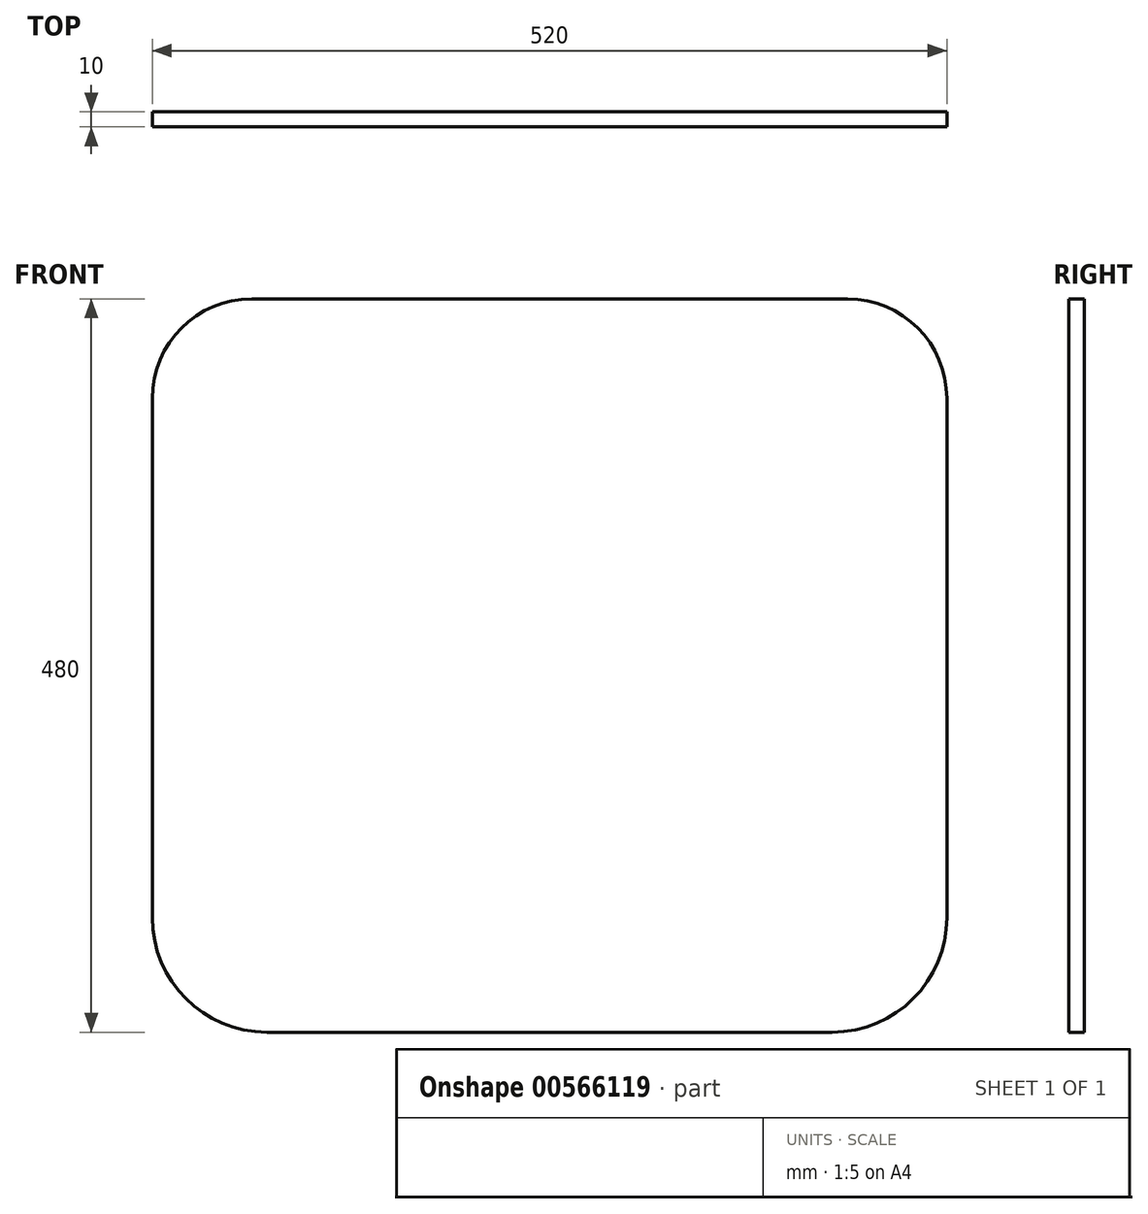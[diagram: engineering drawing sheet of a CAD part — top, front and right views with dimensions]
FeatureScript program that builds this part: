
annotation { "Feature Type Name" : "Feature", "Feature Type Description" : "" }
export const myFeature = defineFeature(function(context is Context, id is Id, definition is map)
    precondition{}
    {
        {
            var Q0;
            Q0=qCreatedBy(makeId("Front.planeOp"),FACE);
            var sketch = newSketch(context, id + "F0", { "sketchPlane" : qUnion([Q0])});
            skPoint(sketch, "E0.middle", {"position": v(0, 0) * mm});
            skPoint(sketch, "E1.visualSharp", {"position": v(-250, 300) * mm});
            skPoint(sketch, "E2.visualSharp", {"position": v(250, 300) * mm});
            skPoint(sketch, "E3.visualSharp", {"position": v(-250, -300) * mm});
            skPoint(sketch, "E4.visualSharp", {"position": v(250, -300) * mm});
            skLineSegment(sketch, "E5.0", {"start": v(260, 105) * mm, "end": v(260, -235) * mm});
            skLineSegment(sketch, "E5.3", {"start": v(-185, -310) * mm, "end": v(185, -310) * mm});
            skArc(sketch, "E5.4", {"start": v(-260, -235) * mm, "mid": v(-238.03, -288.03) * mm, "end": v(-185, -310) * mm});
            skLineSegment(sketch, "E5.5", {"start": v(-260, 105) * mm, "end": v(-260, -235) * mm});
            skArc(sketch, "E6.0", {"start": v(185, -310) * mm, "mid": v(238.03, -288.03) * mm, "end": v(260, -235) * mm});
            skPoint(sketch, "E7.endSnap0", {"position": v(0, 310) * mm});
            skLineSegment(sketch, "E8", {"start": v(0, 0) * mm, "end": v(-260, 0) * mm});
            skLineSegment(sketch, "E9", {"start": v(-195, 170) * mm, "end": v(195, 170) * mm});
            skPoint(sketch, "E10.orphan", {"position": v(-260, 235) * mm});
            skPoint(sketch, "E7.end.orphan", {"position": v(0, 170) * mm});
            skPoint(sketch, "E7.start.orphan", {"position": v(0, 310) * mm});
            skPoint(sketch, "E5.2.start.orphan", {"position": v(-185, 310) * mm});
            skPoint(sketch, "E5.1.end.orphan", {"position": v(185, 310) * mm});
            skPoint(sketch, "E11.visualSharp", {"position": v(-260, 170) * mm});
            skArc(sketch, "E11.filletArc", {"start": v(-195, 170) * mm, "mid": v(-240.96, 150.96) * mm, "end": v(-260, 105) * mm});
            skPoint(sketch, "E12.visualSharp", {"position": v(260, 170) * mm});
            skArc(sketch, "E12.filletArc", {"start": v(260, 105) * mm, "mid": v(240.96, 150.96) * mm, "end": v(195, 170) * mm});
            skSolve(sketch);
        }
        {
            var Q0;
            Q0=qSketchRegion(id+"F0",true);
            extrude(context, id + "F1", {"entities" : qUnion([Q0]), "depth" : 10 * mm, "offsetDistance" : 25 * mm});
        }
    });
